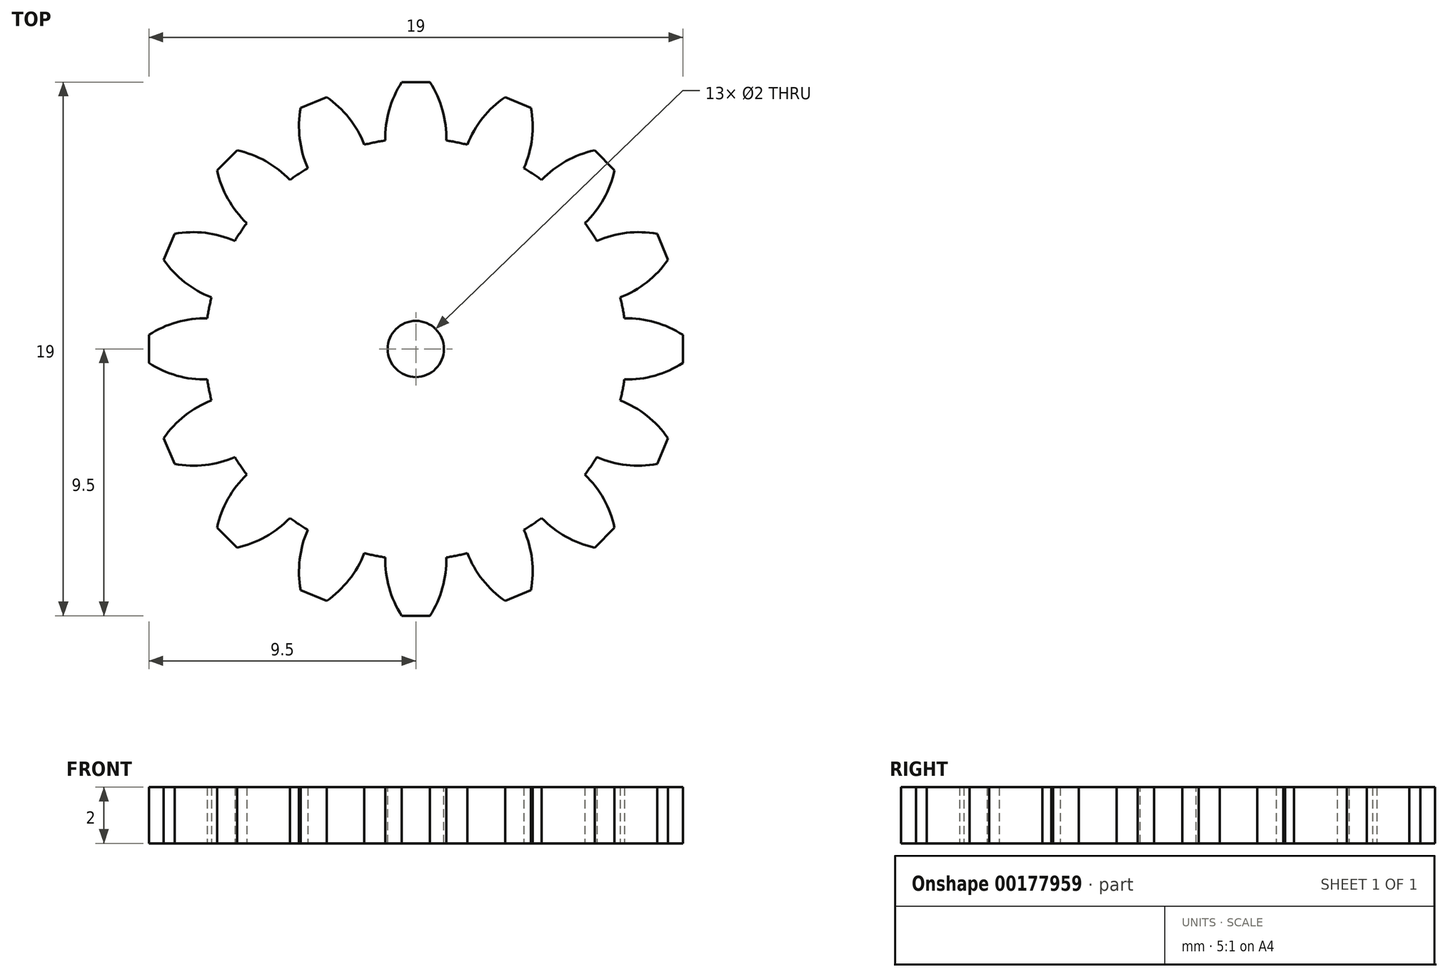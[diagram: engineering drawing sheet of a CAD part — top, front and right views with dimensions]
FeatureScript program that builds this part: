
annotation { "Feature Type Name" : "Feature", "Feature Type Description" : "" }
export const myFeature = defineFeature(function(context is Context, id is Id, definition is map)
    precondition{}
    {
        {
            var Q0;
            Q0=qCreatedBy(makeId("Top.planeOp"),FACE);
            var sketch = newSketch(context, id + "F0", { "sketchPlane" : qUnion([Q0])});
            skCircle(sketch, "E0", {"center": v(0, 0) * mm, "radius": 7.5 * mm});
            skLineSegment(sketch, "E1", {"start": v(0, 0) * mm, "end": v(0, 7.5) * mm, "construction": true});
            skLineSegment(sketch, "E2", {"start": v(0, 9.5) * mm, "end": v(-0.5, 9.5) * mm});
            skArc(sketch, "E3", {"start": v(-0.5, 9.5) * mm, "mid": v(-0.95, 8.5) * mm, "end": v(-1.09, 7.42) * mm});
            skArc(sketch, "E4.MirrorCS", {"start": v(0.5, 9.5) * mm, "mid": v(0.95, 8.5) * mm, "end": v(1.09, 7.42) * mm});
            skLineSegment(sketch, "E5.MirrorCS", {"start": v(0, 9.5) * mm, "end": v(0.5, 9.5) * mm});
            skArc(sketch, "E6.1.0", {"start": v(-4.1, 8.59) * mm, "mid": v(-4.13, 7.5) * mm, "end": v(-3.85, 6.44) * mm});
            skLineSegment(sketch, "E6.1.1", {"start": v(-3.64, 8.78) * mm, "end": v(-4.1, 8.59) * mm});
            skLineSegment(sketch, "E6.1.2", {"start": v(-3.64, 8.78) * mm, "end": v(-3.17, 8.97) * mm});
            skArc(sketch, "E6.1.3", {"start": v(-3.17, 8.97) * mm, "mid": v(-2.38, 8.22) * mm, "end": v(-1.83, 7.27) * mm});
            skArc(sketch, "E6.2.0", {"start": v(-7.07, 6.36) * mm, "mid": v(-6.69, 5.34) * mm, "end": v(-6.02, 4.48) * mm});
            skLineSegment(sketch, "E6.2.1", {"start": v(-6.72, 6.72) * mm, "end": v(-7.07, 6.36) * mm});
            skLineSegment(sketch, "E6.2.2", {"start": v(-6.72, 6.72) * mm, "end": v(-6.36, 7.07) * mm});
            skArc(sketch, "E6.2.3", {"start": v(-6.36, 7.07) * mm, "mid": v(-5.34, 6.69) * mm, "end": v(-4.48, 6.02) * mm});
            skArc(sketch, "E6.3.0", {"start": v(-8.97, 3.17) * mm, "mid": v(-8.22, 2.38) * mm, "end": v(-7.27, 1.83) * mm});
            skLineSegment(sketch, "E6.3.1", {"start": v(-8.78, 3.64) * mm, "end": v(-8.97, 3.17) * mm});
            skLineSegment(sketch, "E6.3.2", {"start": v(-8.78, 3.64) * mm, "end": v(-8.59, 4.1) * mm});
            skArc(sketch, "E6.3.3", {"start": v(-8.59, 4.1) * mm, "mid": v(-7.5, 4.13) * mm, "end": v(-6.44, 3.85) * mm});
            skArc(sketch, "E6.4.0", {"start": v(-9.5, -0.5) * mm, "mid": v(-8.5, -0.95) * mm, "end": v(-7.42, -1.09) * mm});
            skLineSegment(sketch, "E6.4.1", {"start": v(-9.5, 0) * mm, "end": v(-9.5, -0.5) * mm});
            skLineSegment(sketch, "E6.4.2", {"start": v(-9.5, 0) * mm, "end": v(-9.5, 0.5) * mm});
            skArc(sketch, "E6.4.3", {"start": v(-9.5, 0.5) * mm, "mid": v(-8.5, 0.95) * mm, "end": v(-7.42, 1.09) * mm});
            skArc(sketch, "E6.5.0", {"start": v(-8.59, -4.1) * mm, "mid": v(-7.5, -4.13) * mm, "end": v(-6.44, -3.85) * mm});
            skLineSegment(sketch, "E6.5.1", {"start": v(-8.78, -3.64) * mm, "end": v(-8.59, -4.1) * mm});
            skLineSegment(sketch, "E6.5.2", {"start": v(-8.78, -3.64) * mm, "end": v(-8.97, -3.17) * mm});
            skArc(sketch, "E6.5.3", {"start": v(-8.97, -3.17) * mm, "mid": v(-8.22, -2.38) * mm, "end": v(-7.27, -1.83) * mm});
            skArc(sketch, "E6.6.0", {"start": v(-6.36, -7.07) * mm, "mid": v(-5.34, -6.69) * mm, "end": v(-4.48, -6.02) * mm});
            skLineSegment(sketch, "E6.6.1", {"start": v(-6.72, -6.72) * mm, "end": v(-6.36, -7.07) * mm});
            skLineSegment(sketch, "E6.6.2", {"start": v(-6.72, -6.72) * mm, "end": v(-7.07, -6.36) * mm});
            skArc(sketch, "E6.6.3", {"start": v(-7.07, -6.36) * mm, "mid": v(-6.69, -5.34) * mm, "end": v(-6.02, -4.48) * mm});
            skArc(sketch, "E6.7.0", {"start": v(-3.17, -8.97) * mm, "mid": v(-2.38, -8.22) * mm, "end": v(-1.83, -7.27) * mm});
            skLineSegment(sketch, "E6.7.1", {"start": v(-3.64, -8.78) * mm, "end": v(-3.17, -8.97) * mm});
            skLineSegment(sketch, "E6.7.2", {"start": v(-3.64, -8.78) * mm, "end": v(-4.1, -8.59) * mm});
            skArc(sketch, "E6.7.3", {"start": v(-4.1, -8.59) * mm, "mid": v(-4.13, -7.5) * mm, "end": v(-3.85, -6.44) * mm});
            skArc(sketch, "E6.8.0", {"start": v(0.5, -9.5) * mm, "mid": v(0.95, -8.5) * mm, "end": v(1.09, -7.42) * mm});
            skLineSegment(sketch, "E6.8.1", {"start": v(0, -9.5) * mm, "end": v(0.5, -9.5) * mm});
            skLineSegment(sketch, "E6.8.2", {"start": v(0, -9.5) * mm, "end": v(-0.5, -9.5) * mm});
            skArc(sketch, "E6.8.3", {"start": v(-0.5, -9.5) * mm, "mid": v(-0.95, -8.5) * mm, "end": v(-1.09, -7.42) * mm});
            skArc(sketch, "E6.9.0", {"start": v(4.1, -8.59) * mm, "mid": v(4.13, -7.5) * mm, "end": v(3.85, -6.44) * mm});
            skLineSegment(sketch, "E6.9.1", {"start": v(3.64, -8.78) * mm, "end": v(4.1, -8.59) * mm});
            skLineSegment(sketch, "E6.9.2", {"start": v(3.64, -8.78) * mm, "end": v(3.17, -8.97) * mm});
            skArc(sketch, "E6.9.3", {"start": v(3.17, -8.97) * mm, "mid": v(2.38, -8.22) * mm, "end": v(1.83, -7.27) * mm});
            skArc(sketch, "E6.10.0", {"start": v(7.07, -6.36) * mm, "mid": v(6.69, -5.34) * mm, "end": v(6.02, -4.48) * mm});
            skLineSegment(sketch, "E6.10.1", {"start": v(6.72, -6.72) * mm, "end": v(7.07, -6.36) * mm});
            skLineSegment(sketch, "E6.10.2", {"start": v(6.72, -6.72) * mm, "end": v(6.36, -7.07) * mm});
            skArc(sketch, "E6.10.3", {"start": v(6.36, -7.07) * mm, "mid": v(5.34, -6.69) * mm, "end": v(4.48, -6.02) * mm});
            skArc(sketch, "E6.11.0", {"start": v(8.97, -3.17) * mm, "mid": v(8.22, -2.38) * mm, "end": v(7.27, -1.83) * mm});
            skLineSegment(sketch, "E6.11.1", {"start": v(8.78, -3.64) * mm, "end": v(8.97, -3.17) * mm});
            skLineSegment(sketch, "E6.11.2", {"start": v(8.78, -3.64) * mm, "end": v(8.59, -4.1) * mm});
            skArc(sketch, "E6.11.3", {"start": v(8.59, -4.1) * mm, "mid": v(7.5, -4.13) * mm, "end": v(6.44, -3.85) * mm});
            skArc(sketch, "E6.12.0", {"start": v(9.5, 0.5) * mm, "mid": v(8.5, 0.95) * mm, "end": v(7.42, 1.09) * mm});
            skLineSegment(sketch, "E6.12.1", {"start": v(9.5, 0) * mm, "end": v(9.5, 0.5) * mm});
            skLineSegment(sketch, "E6.12.2", {"start": v(9.5, 0) * mm, "end": v(9.5, -0.5) * mm});
            skArc(sketch, "E6.12.3", {"start": v(9.5, -0.5) * mm, "mid": v(8.5, -0.95) * mm, "end": v(7.42, -1.09) * mm});
            skArc(sketch, "E6.13.0", {"start": v(8.59, 4.1) * mm, "mid": v(7.5, 4.13) * mm, "end": v(6.44, 3.85) * mm});
            skLineSegment(sketch, "E6.13.1", {"start": v(8.78, 3.64) * mm, "end": v(8.59, 4.1) * mm});
            skLineSegment(sketch, "E6.13.2", {"start": v(8.78, 3.64) * mm, "end": v(8.97, 3.17) * mm});
            skArc(sketch, "E6.13.3", {"start": v(8.97, 3.17) * mm, "mid": v(8.22, 2.38) * mm, "end": v(7.27, 1.83) * mm});
            skArc(sketch, "E6.14.0", {"start": v(6.36, 7.07) * mm, "mid": v(5.34, 6.69) * mm, "end": v(4.48, 6.02) * mm});
            skLineSegment(sketch, "E6.14.1", {"start": v(6.72, 6.72) * mm, "end": v(6.36, 7.07) * mm});
            skLineSegment(sketch, "E6.14.2", {"start": v(6.72, 6.72) * mm, "end": v(7.07, 6.36) * mm});
            skArc(sketch, "E6.14.3", {"start": v(7.07, 6.36) * mm, "mid": v(6.69, 5.34) * mm, "end": v(6.02, 4.48) * mm});
            skArc(sketch, "E6.15.0", {"start": v(3.17, 8.97) * mm, "mid": v(2.38, 8.22) * mm, "end": v(1.83, 7.27) * mm});
            skLineSegment(sketch, "E6.15.1", {"start": v(3.64, 8.78) * mm, "end": v(3.17, 8.97) * mm});
            skLineSegment(sketch, "E6.15.2", {"start": v(3.64, 8.78) * mm, "end": v(4.1, 8.59) * mm});
            skArc(sketch, "E6.15.3", {"start": v(4.1, 8.59) * mm, "mid": v(4.13, 7.5) * mm, "end": v(3.85, 6.44) * mm});
            skSolve(sketch);
        }
        {
            var Q0;
            Q0 = qSketchRegion(id + "F0", true);
            extrude(context, id + "F1", {"entities" : qUnion([Q0]), "depth" : 2 * mm});
        }
        {
            var Q0;
            Q0=makeQuery(id+"F1.opExtrude","CAP_FACE",FACE,{"disambiguationData":[OSD([sQuery(id+"F0.wireOp",EDGE,"E0"),sQuery(id+"F0.wireOp",EDGE,"E2"),sQuery(id+"F0.wireOp",EDGE,"E3"),sQuery(id+"F0.wireOp",EDGE,"E4.MirrorCS"),sQuery(id+"F0.wireOp",EDGE,"E5.MirrorCS"),sQuery(id+"F0.wireOp",EDGE,"E6.1.0"),sQuery(id+"F0.wireOp",EDGE,"E6.1.1"),sQuery(id+"F0.wireOp",EDGE,"E6.1.2"),sQuery(id+"F0.wireOp",EDGE,"E6.1.3"),sQuery(id+"F0.wireOp",EDGE,"E6.2.0"),sQuery(id+"F0.wireOp",EDGE,"E6.2.1"),sQuery(id+"F0.wireOp",EDGE,"E6.2.2"),sQuery(id+"F0.wireOp",EDGE,"E6.2.3"),sQuery(id+"F0.wireOp",EDGE,"E6.3.0"),sQuery(id+"F0.wireOp",EDGE,"E6.3.1"),sQuery(id+"F0.wireOp",EDGE,"E6.3.2"),sQuery(id+"F0.wireOp",EDGE,"E6.3.3"),sQuery(id+"F0.wireOp",EDGE,"E6.4.0"),sQuery(id+"F0.wireOp",EDGE,"E6.4.1"),sQuery(id+"F0.wireOp",EDGE,"E6.4.2"),sQuery(id+"F0.wireOp",EDGE,"E6.4.3"),sQuery(id+"F0.wireOp",EDGE,"E6.5.0"),sQuery(id+"F0.wireOp",EDGE,"E6.5.1"),sQuery(id+"F0.wireOp",EDGE,"E6.5.2"),sQuery(id+"F0.wireOp",EDGE,"E6.5.3"),sQuery(id+"F0.wireOp",EDGE,"E6.6.0"),sQuery(id+"F0.wireOp",EDGE,"E6.6.1"),sQuery(id+"F0.wireOp",EDGE,"E6.6.2"),sQuery(id+"F0.wireOp",EDGE,"E6.6.3"),sQuery(id+"F0.wireOp",EDGE,"E6.7.0"),sQuery(id+"F0.wireOp",EDGE,"E6.7.1"),sQuery(id+"F0.wireOp",EDGE,"E6.7.2"),sQuery(id+"F0.wireOp",EDGE,"E6.7.3"),sQuery(id+"F0.wireOp",EDGE,"E6.8.0"),sQuery(id+"F0.wireOp",EDGE,"E6.8.1"),sQuery(id+"F0.wireOp",EDGE,"E6.8.2"),sQuery(id+"F0.wireOp",EDGE,"E6.8.3"),sQuery(id+"F0.wireOp",EDGE,"E6.9.0"),sQuery(id+"F0.wireOp",EDGE,"E6.9.1"),sQuery(id+"F0.wireOp",EDGE,"E6.9.2"),sQuery(id+"F0.wireOp",EDGE,"E6.9.3"),sQuery(id+"F0.wireOp",EDGE,"E6.10.0"),sQuery(id+"F0.wireOp",EDGE,"E6.10.1"),sQuery(id+"F0.wireOp",EDGE,"E6.10.2"),sQuery(id+"F0.wireOp",EDGE,"E6.10.3"),sQuery(id+"F0.wireOp",EDGE,"E6.11.0"),sQuery(id+"F0.wireOp",EDGE,"E6.11.1"),sQuery(id+"F0.wireOp",EDGE,"E6.11.2"),sQuery(id+"F0.wireOp",EDGE,"E6.11.3"),sQuery(id+"F0.wireOp",EDGE,"E6.12.0"),sQuery(id+"F0.wireOp",EDGE,"E6.12.1"),sQuery(id+"F0.wireOp",EDGE,"E6.12.2"),sQuery(id+"F0.wireOp",EDGE,"E6.12.3"),sQuery(id+"F0.wireOp",EDGE,"E6.13.0"),sQuery(id+"F0.wireOp",EDGE,"E6.13.1"),sQuery(id+"F0.wireOp",EDGE,"E6.13.2"),sQuery(id+"F0.wireOp",EDGE,"E6.13.3"),sQuery(id+"F0.wireOp",EDGE,"E6.14.0"),sQuery(id+"F0.wireOp",EDGE,"E6.14.1"),sQuery(id+"F0.wireOp",EDGE,"E6.14.2"),sQuery(id+"F0.wireOp",EDGE,"E6.14.3"),sQuery(id+"F0.wireOp",EDGE,"E6.15.0"),sQuery(id+"F0.wireOp",EDGE,"E6.15.1"),sQuery(id+"F0.wireOp",EDGE,"E6.15.2"),sQuery(id+"F0.wireOp",EDGE,"E6.15.3")])],"isStart":false});
            var sketch = newSketch(context, id + "F2", { "sketchPlane" : qUnion([Q0])});
            skCircle(sketch, "E7", {"center": v(0, 0) * mm, "radius": 1 * mm});
            skSolve(sketch);
        }
        {
            var Q0;
            Q0 = qSketchRegion(id + "F2", true);
            extrude(context, id + "F3", {"entities" : qUnion([Q0]), "operationType" : NewBodyOperationType.REMOVE, "endBound" : BoundingType.THROUGH_ALL, "oppositeDirection" : true, "depth" : 25 * mm});
        }
    });
